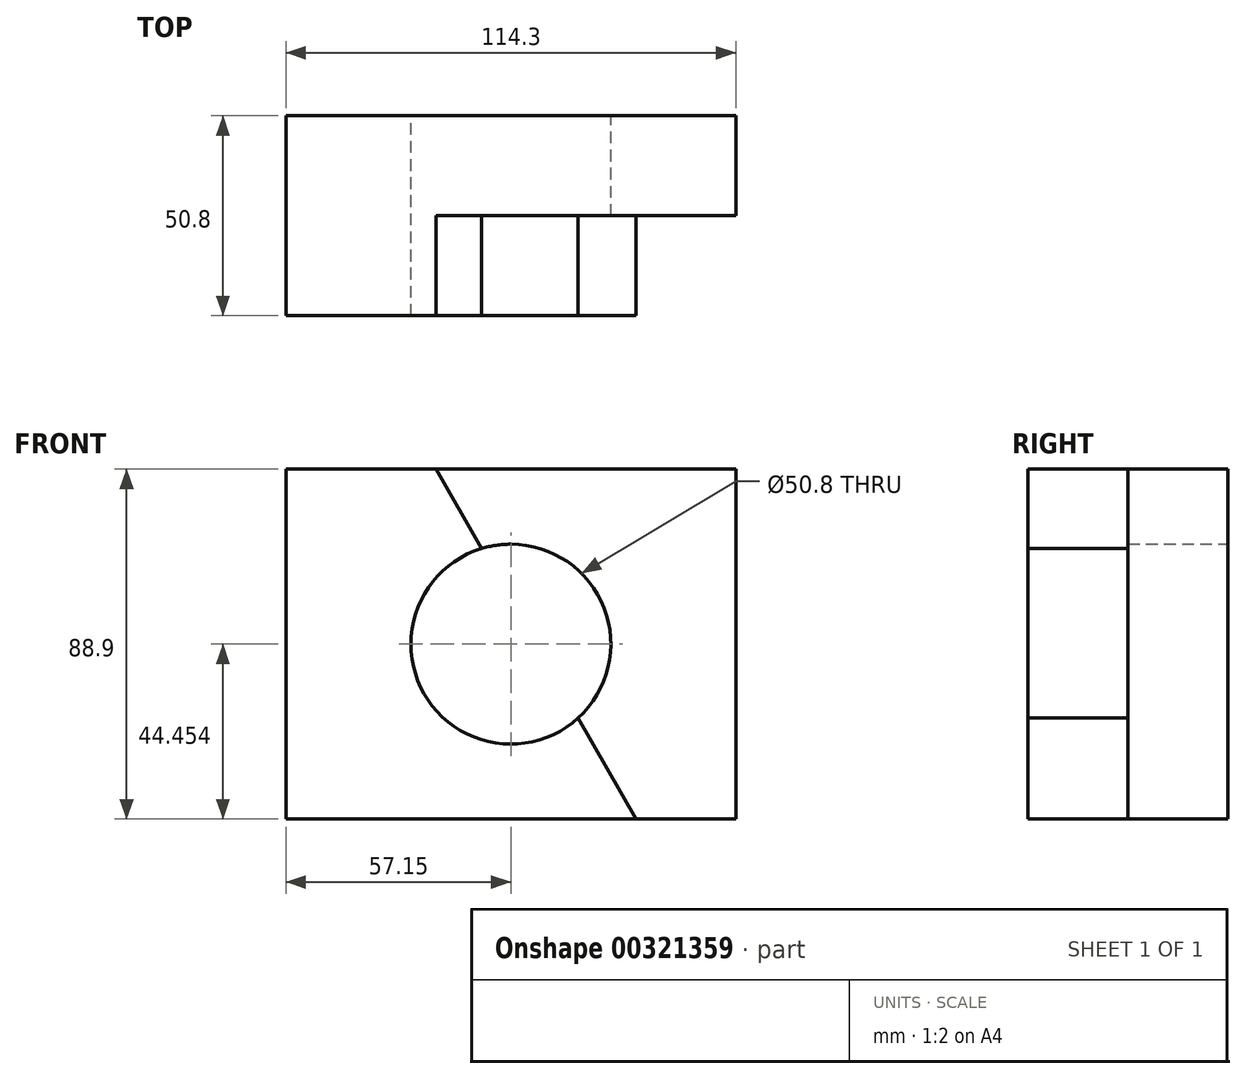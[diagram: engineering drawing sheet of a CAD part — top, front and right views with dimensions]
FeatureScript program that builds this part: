
annotation { "Feature Type Name" : "Feature", "Feature Type Description" : "" }
export const myFeature = defineFeature(function(context is Context, id is Id, definition is map)
    precondition{}
    {
        {
            var Q0;
            Q0=qCreatedBy(makeId("Front.planeOp"),FACE);
            var sketch = newSketch(context, id + "F0", { "sketchPlane" : qUnion([Q0])});
            skLineSegment(sketch, "E0.bottom", {"start": v(-57.15, 37.82) * mm, "end": v(57.15, 37.82) * mm});
            skLineSegment(sketch, "E0.top", {"start": v(-57.15, -51.08) * mm, "end": v(57.15, -51.08) * mm});
            skLineSegment(sketch, "E0.left", {"start": v(-57.15, 37.82) * mm, "end": v(-57.15, -51.08) * mm});
            skLineSegment(sketch, "E0.right", {"start": v(57.15, 37.82) * mm, "end": v(57.15, -51.08) * mm});
            skSolve(sketch);
        }
        {
            var Q0;
            Q0=makeQuery(id+"F0.imprint","IMPRINT",FACE,{"disambiguationData":[TD([[makeQuery(id+"F0.imprint","IMPRINT",EDGE,{"derivedFrom":sQuery(id+"F0.wireOp",EDGE,"E0.bottom")}),-1.0]])]});
            var Q1;
            Q1 = qSketchRegion(id + "F2", true);
            extrude(context, id + "F1", {"entities" : qUnion([Q0, Q1]), "depth" : 25.4 * mm});
        }
        {
            var Q0;
            Q0=makeQuery(id+"F1.opExtrude","CAP_FACE",FACE,{"disambiguationData":[OSD([sQuery(id+"F0.wireOp",EDGE,"E0.bottom"),sQuery(id+"F0.wireOp",EDGE,"E0.top"),sQuery(id+"F0.wireOp",EDGE,"E0.left"),sQuery(id+"F0.wireOp",EDGE,"E0.right")])],"isStart":false});
            var sketch = newSketch(context, id + "F2", { "sketchPlane" : qUnion([Q0])});
            skLineSegment(sketch, "E1", {"start": v(-19.05, 37.82) * mm, "end": v(31.75, -51.08) * mm});
            skSolve(sketch);
        }
        {
            var Q0;
            {var subQ0=sQuery(id+"F2.wireOp",EDGE,"E1");Q0=makeQuery(id+"F2.imprint","IMPRINT",FACE,{"disambiguationData":[TD([[makeQuery(id+"F2.imprint","IMPRINT",EDGE,{"derivedFrom":subQ0}),-1.0]])]});}
            extrude(context, id + "F3", {"entities" : qUnion([Q0]), "operationType" : NewBodyOperationType.ADD, "depth" : 25.4 * mm});
        }
        {
            var Q0;
            Q0=makeQuery(id+"F1.opExtrude","CAP_FACE",FACE,{"disambiguationData":[OSD([sQuery(id+"F0.wireOp",EDGE,"E0.bottom"),sQuery(id+"F0.wireOp",EDGE,"E0.top"),sQuery(id+"F0.wireOp",EDGE,"E0.left"),sQuery(id+"F0.wireOp",EDGE,"E0.right")])],"isStart":true});
            var sketch = newSketch(context, id + "F4", { "sketchPlane" : qUnion([Q0])});
            skPoint(sketch, "E2.endSnap0", {"position": v(-57.15, -6.63) * mm});
            skCircle(sketch, "E3", {"center": v(0, -6.63) * mm, "radius": 25.4 * mm});
            skSolve(sketch);
        }
        {
            var Q0;
            Q0=makeQuery(id+"F4.imprint","IMPRINT",FACE,{"disambiguationData":[TD([[makeQuery(id+"F4.imprint","IMPRINT",EDGE,{"derivedFrom":sQuery(id+"F4.wireOp",EDGE,"E3")}),1.0]])]});
            extrude(context, id + "F5", {"entities" : qUnion([Q0]), "operationType" : NewBodyOperationType.REMOVE, "endBound" : BoundingType.THROUGH_ALL, "oppositeDirection" : true, "depth" : 25.4 * mm});
        }
    });
